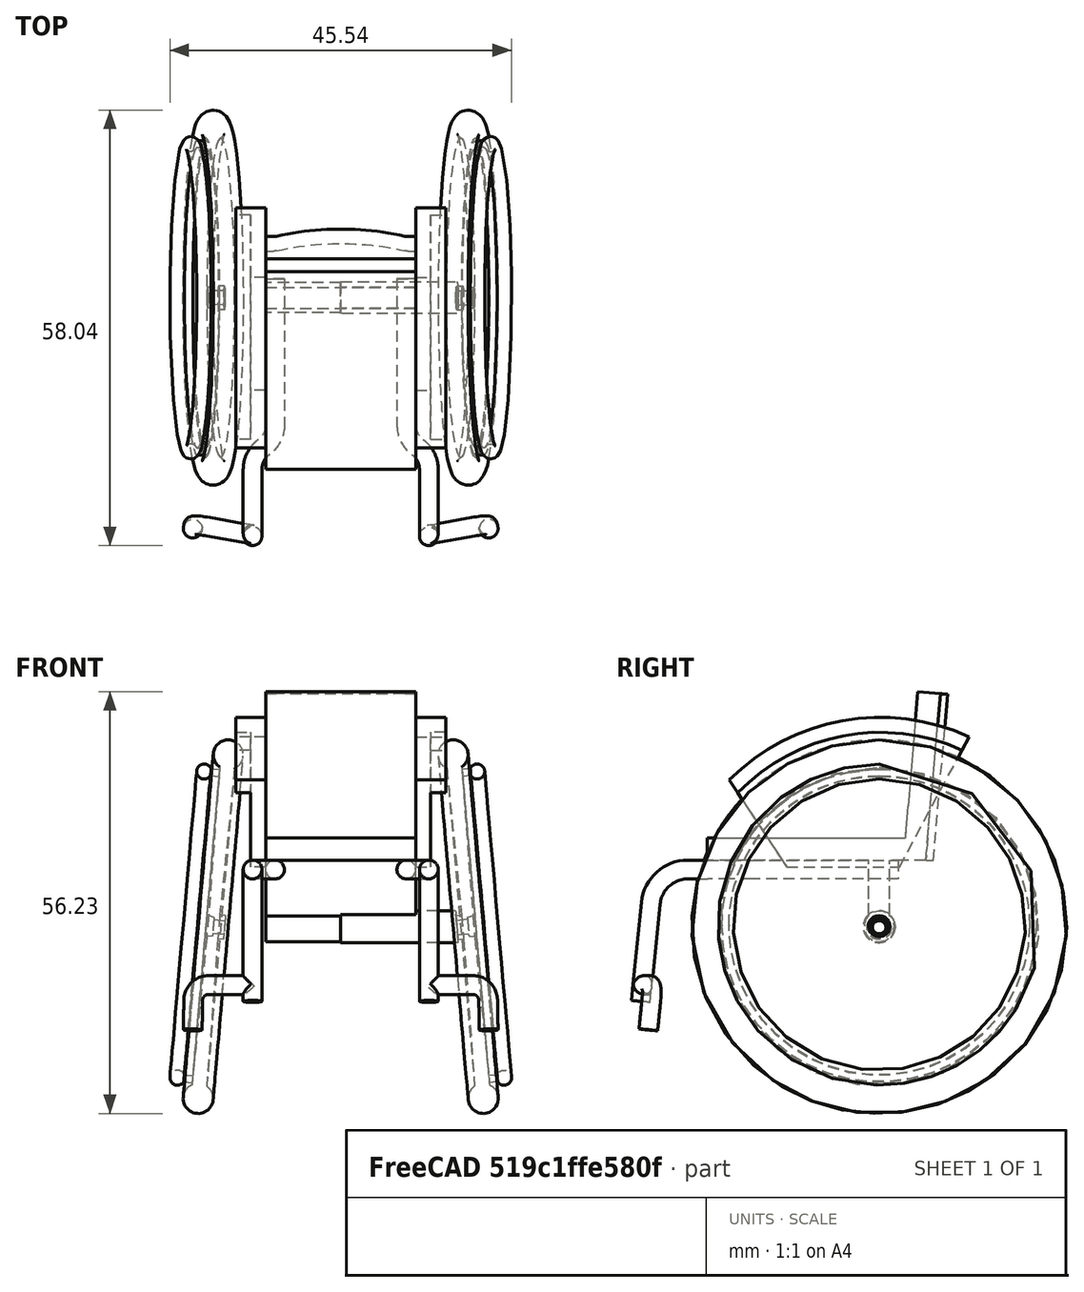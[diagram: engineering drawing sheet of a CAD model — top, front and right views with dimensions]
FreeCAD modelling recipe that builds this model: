
FCSTD DOCUMENT  (FreeCAD 2021.0205R23662 +3201 (Git))
Label: ToyWheelchair_02_mirrored
License: All rights reserved
LicenseURL: http://en.wikipedia.org/wiki/All_rights_reserved
objects: Sketcher::SketchObject×15, PartDesign::Plane×8, PartDesign::Body×5, PartDesign::Pad×5, PartDesign::ShapeBinder×4, PartDesign::AdditivePipe×3, PartDesign::Mirrored×3, PartDesign::Revolution×1, Spreadsheet::Sheet×1, PartDesign::Point×1
note: 66 computed .brp shape members not serialized (recipe doc carries the construction recipe); baked Part::Feature solids carry a one-line shape summary decoded from their .brp

FEATURE [Sketcher::SketchObject] Sketch  label="MASTER.Sketch"
  FullyConstrained = false
  MapMode = 5
  Placement = pos=(0,0,0) rot=(0.57735,0.57735,0.57735;2.0944rad)
  Support = -> [YZ_Plane]
  expr: Constraints[29] = cos(Spreadsheet.WheelAngle) * Spreadsheet.WheelDiameter
  expr: Constraints[36] = Spreadsheet.WheelDiameter
  sketch-geometry (15):
    g0: Circle CenterX=0 CenterY=24.9049 CenterZ=0 NormalX=0 NormalY=0 NormalZ=1 AngleXU=0 Radius=2.63162
    g1: LineSegment StartX=-6.93783 StartY=34.5214 StartZ=0 EndX=28.2394 EndY=34.5214 EndZ=0
    g2: LineSegment StartX=0 StartY=32.5214 StartZ=0 EndX=-25.4861 EndY=32.5214 EndZ=0
    g3: LineSegment StartX=-30.46 StartY=28.031 StartZ=0 EndX=-32 EndY=13 EndZ=0
    g4: LineSegment StartX=-32 StartY=13 StartZ=0 EndX=-29 EndY=5 EndZ=0
    g5: Circle CenterX=-29 CenterY=5 CenterZ=0 NormalX=0 NormalY=0 NormalZ=1 AngleXU=0 Radius=5
    g6: LineSegment [constr] StartX=-29 StartY=5 StartZ=0 EndX=-29 EndY=12.0907 EndZ=0
    g7: ArcOfCircle CenterX=-25.4861 CenterY=27.5214 CenterZ=0 NormalX=0 NormalY=0 NormalZ=1 AngleXU=0 Radius=5 StartAngle=1.5708 EndAngle=3.0395
    g8: LineSegment [constr] StartX=-25.4861 StartY=32.5214 StartZ=0 EndX=-32.1716 EndY=32.5214 EndZ=0
    g9: LineSegment [constr] StartX=-30.46 StartY=28.031 StartZ=0 EndX=-29.1955 EndY=40.3737 EndZ=0
    g10: GeomPoint [constr] X=-30 Y=32.5214 Z=0
    g11: LineSegment StartX=0 StartY=0 StartZ=0 EndX=0 EndY=24.9049 EndZ=0
    g12: LineSegment StartX=0 StartY=24.9049 StartZ=0 EndX=0 EndY=49.8097 EndZ=0
    g13: LineSegment StartX=-25 StartY=24.9049 StartZ=0 EndX=0 EndY=24.9049 EndZ=0
    g14: LineSegment StartX=0 StartY=24.9049 StartZ=0 EndX=25 EndY=24.9049 EndZ=0
  constraints (37):
    c: Horizontal(g1)
    c: DistanceY(g-1,g1) = 34.5214
    c: Horizontal(g2)
    c: Coincident(g4,g3)
    c: Coincident(g5,g4)
    c: Tangent(g5,g-1)
    c: Diameter(g5) = 10
    c: Coincident(g6,g4)
    c: Vertical(g6)
    c: DistanceY(g4,g3) = 8
    c: DistanceX(g3,g4) = 3
    c: Tangent(g2,g7) = -1.5708
    c: Tangent(g3,g7) = -1.5708
    c: Radius(g7) = 5
    c: DistanceY(g2,g1) = 2
    c: PointOnObject(g2,g-2)
    c: Coincident(g8,g2)
    c: Horizontal(g8)
    c: Coincident(g9,g3)
    c: Tangent(g9,g7)
    c: PointOnObject(g10,g8)
    c: PointOnObject(g10,g9)
    c: DistanceX(g10,g-1) = 30
    c: DistanceX(g3,g10) = 2
    c: Coincident(g11,g-1)
    c: Coincident(g11,g0)
    c: Vertical(g11)
    c: Coincident(g12,g0)
    c: PointOnObject(g12,g-2)
    c: Distance(g11,g12) = 49.8097
    c: Coincident(g13,g0)
    c: Horizontal(g13)
    c: Coincident(g14,g0)
    c: Horizontal(g14)
    c: Equal(g12,g11)
    c: Equal(g13,g14)
    c: Distance(g13,g14) = 50
FEATURE [Sketcher::SketchObject] Sketch001  label="Sketch.Wheel.Angle"
  FullyConstrained = true
  MapMode = 5
  Placement = pos=(0,0,0) rot=(1,0,0;1.5708rad)
  Support = -> [XZ_Plane]
  expr: Constraints[4] = Spreadsheet.SeatWidth / 2 + 7
  expr: Constraints[6] = 50mm
  sketch-geometry (3):
    g0: LineSegment StartX=19.1789 StartY=0 StartZ=0 EndX=14.8211 EndY=49.8097 EndZ=0
    g1: Circle [constr] CenterX=17 CenterY=24.9049 CenterZ=0 NormalX=0 NormalY=0 NormalZ=1 AngleXU=0 Radius=25
    g2: GeomPoint [constr] X=14.8211 Y=49.8097 Z=0
  constraints (8):
    c: PointOnObject(g0,g-1)
    c: PointOnObject(g1,g0)
    c: PointOnObject(g0,g1)
    c: PointOnObject(g0,g1)
    c: DistanceX(g-1,g1) = 17
    c: Angle(g-2,g0) = 0.0872665
    c: Distance(g0) = 50
    c: Coincident(g2,g0)
FEATURE [PartDesign::Body] Body  label="MASTER.Body"
  AutoGroupSolids = false
  ExportMode = 0
  Group = -> [Sketch001,Sketch]
  Origin = -> Origin
  _ExportChildren = -> [Sketch001,Sketch]
  _GroupVersion = 1
FEATURE [PartDesign::ShapeBinder] ShapeBinder
  Placement = pos=(0,0,0) rot=(0.57735,0.57735,0.57735;2.0944rad)
  Support = -> [Sketch]
  TraceSupport = false
FEATURE [PartDesign::Plane] DatumPlane
  AttachmentOffset = pos=(0,0,10) rot=(0,0,1;0rad)
  Length = 10
  MapMode = 5
  MinimumLength = 10
  MinimumWidth = 10
  Placement = pos=(10,-2.2e-15,2.2e-15) rot=(0.57735,0.57735,0.57735;2.0944rad)
  ResizeMode = 0
  Support = -> [YZ_Plane001]
  Width = 10
  expr: .AttachmentOffset.Base.z = Spreadsheet.SeatWidth / 2
FEATURE [Sketcher::SketchObject] Sketch002
  ExternalGeometry = -> [ShapeBinder]
  FullyConstrained = false
  MapMode = 5
  Placement = pos=(10,-2.2e-15,2.2e-15) rot=(0.57735,0.57735,0.57735;2.0944rad)
  Support = -> [DatumPlane]
  expr: Constraints[10] = Spreadsheet.WheelDiameter
  sketch-geometry (10):
    g0: LineSegment StartX=-20 StartY=44.4492 StartZ=0 EndX=-12.3537 EndY=32.8577 EndZ=0
    g1: LineSegment StartX=-12.3537 StartY=32.8577 StartZ=0 EndX=2.70695 EndY=32.8577 EndZ=0
    g2: LineSegment StartX=2.70695 StartY=32.8577 StartZ=0 EndX=12 EndY=50.201 EndZ=0
    g3: ArcOfCircle CenterX=0.114642 CenterY=24.4333 CenterZ=0 NormalX=0 NormalY=0 NormalZ=1 AngleXU=0 Radius=28.3767 StartAngle=1.13863 EndAngle=2.35865
    g4: GeomPoint [constr] X=10.3723 Y=47.1634 Z=0
    g5: GeomPoint [constr] X=0 Y=52.8097 Z=0
    g6: Circle [constr] CenterX=1.1e-15 CenterY=24.9049 CenterZ=0 NormalX=0 NormalY=0 NormalZ=1 AngleXU=0 Radius=25
    g7: GeomPoint [constr] X=-18.3252 Y=41.9103 Z=0
    g8: Circle [constr] CenterX=-19.174 CenterY=43.1971 CenterZ=0 NormalX=0 NormalY=0 NormalZ=1 AngleXU=0 Radius=1.5
    g9: Circle [constr] CenterX=11.2916 CenterY=48.8788 CenterZ=0 NormalX=0 NormalY=0 NormalZ=1 AngleXU=0 Radius=1.5
  constraints (23):
    c: Coincident(g0,g1)
    c: Horizontal(g1)
    c: Coincident(g1,g2)
    c: Coincident(g3,g2)
    c: Coincident(g3,g0)
    c: PointOnObject(g4,g2)
    c: PointOnObject(g5,g-2)
    c: PointOnObject(g5,g3)
    c: Distance(g-3,g5) = 3
    c: Coincident(g6,g-3)
    c: Diameter(g6) = 50
    c: PointOnObject(g7,g6)
    c: PointOnObject(g7,g0)
    c: DistanceX(g5,g2) = 12
    c: DistanceX(g0,g5) = 20
    c: PointOnObject(g8,g0)
    c: PointOnObject(g0,g8)
    c: PointOnObject(g9,g2)
    c: PointOnObject(g2,g9)
    c: Tangent(g9,g6)
    c: Tangent(g8,g6)
    c: Equal(g8,g9)
    c: Diameter(g9) = 3
FEATURE [PartDesign::Pad] Pad
  ClaimChildren = false
  Direction = (1,1,1)
  Fit = 0
  FitJoin = 0
  InnerFit = 0
  InnerFitJoin = 0
  InnerTaperAngle = 0
  InnerTaperAngleRev = 0
  Length = 2
  Length2 = 100
  NewSolid = false
  Placement = pos=(10,-2.2e-15,2.2e-15) rot=(0.57735,0.57735,0.57735;2.0944rad)
  Profile = -> Sketch002
  Suppress = false
  Type = 0
FEATURE [PartDesign::ShapeBinder] ShapeBinder001
  Placement = pos=(0,0,0) rot=(1,0,0;1.5708rad)
  Support = -> [Sketch001]
  TraceSupport = false
FEATURE [Sketcher::SketchObject] Sketch003
  ExternalGeometry = -> [ShapeBinder001]
  FullyConstrained = false
  MapMode = 5
  Placement = pos=(0,0,0) rot=(1,0,0;1.5708rad)
  Support = -> [XZ_Plane002]
  sketch-geometry (20):
    g0: Circle [constr] CenterX=17 CenterY=24.9049 CenterZ=0 NormalX=0 NormalY=0 NormalZ=1 AngleXU=0 Radius=25
    g1: ArcOfCircle CenterX=14.9954 CenterY=47.8173 CenterZ=0 NormalX=0 NormalY=0 NormalZ=1 AngleXU=0 Radius=2 StartAngle=5.32325 EndAngle=10.5592
    g2: LineSegment StartX=15.3663 StartY=26.368 StartZ=0 EndX=16.1134 EndY=26.4334 EndZ=0
    g3: LineSegment [constr] StartX=18.3548 StartY=26.6295 StartZ=0 EndX=18.4943 EndY=25.0356 EndZ=0
    g4: LineSegment [constr] StartX=18.4943 StartY=25.0356 StartZ=0 EndX=15.5057 EndY=24.7741 EndZ=0
    g5: LineSegment [constr] StartX=15.5057 StartY=24.7741 StartZ=0 EndX=15.3663 EndY=26.368 EndZ=0
    g6: LineSegment StartX=16.1426 StartY=46.179 StartZ=0 EndX=16.1661 EndY=45.8642 EndZ=0
    g7: LineSegment StartX=14.1502 StartY=46.0047 StartZ=0 EndX=16.1134 EndY=26.4334 EndZ=0
    g8: ArcOfCircle CenterX=18.2028 CenterY=45.5778 CenterZ=0 NormalX=0 NormalY=0 NormalZ=1 AngleXU=0 Radius=1 StartAngle=3.71006 EndAngle=9.03084
    g9: LineSegment [constr] StartX=18.2028 StartY=45.5778 StartZ=0 EndX=15.2142 EndY=45.3163 EndZ=0
    g10: LineSegment StartX=17.2794 StartY=45.9616 StartZ=0 EndX=16.1661 EndY=45.8642 EndZ=0
    g11: LineSegment StartX=17.3601 StartY=45.0395 StartZ=0 EndX=16.235 EndY=44.941 EndZ=0
    g12: LineSegment StartX=16.235 StartY=44.941 StartZ=0 EndX=17.6077 EndY=26.5641 EndZ=0
    g13: LineSegment [constr] StartX=16.1661 StartY=45.8642 StartZ=0 EndX=16.235 EndY=44.941 EndZ=0
    g14: LineSegment StartX=16.8909 StartY=26.1514 StartZ=0 EndX=16.916 EndY=25.8649 EndZ=0
    g15: LineSegment StartX=16.916 StartY=25.8649 StartZ=0 EndX=15.4261 EndY=25.6845 EndZ=0
    g16: LineSegment StartX=15.4261 StartY=25.6845 StartZ=0 EndX=15.3663 EndY=26.368 EndZ=0
    g17: LineSegment StartX=16.8909 StartY=26.1514 StartZ=0 EndX=17.6214 EndY=26.3806 EndZ=0
    g18: LineSegment StartX=17.6077 StartY=26.5641 StartZ=0 EndX=17.6214 EndY=26.3806 EndZ=0
    g19: LineSegment [constr] StartX=15.3663 StartY=26.368 StartZ=0 EndX=18.3548 EndY=26.6295 EndZ=0
  constraints (54):
    c: PointOnObject(g0,g-3)
    c: PointOnObject(g-3,g0)
    c: PointOnObject(g-3,g0)
    c: PointOnObject(g-3,g1)
    c: Coincident(g3,g4)
    c: Coincident(g4,g5)
    c: Coincident(g5,g2)
    c: PointOnObject(g0,g4)
    c: Perpendicular(g5,g4)
    c: Perpendicular(g-3,g4)
    c: Perpendicular(g3,g4)
    c: Symmetric(g2,g3,g-3)
    c: Symmetric(g7,g12,g-3)
    c: Symmetric(g6,g7,g-3)
    c: Coincident(g1,g6)
    c: Coincident(g1,g7)
    c: PointOnObject(g2,g7)
    c: Diameter(g1) = 4
    c: Distance(g1,g1) = 2
    c: Distance(g2,g12) = 1.5
    c: Distance(g2,g3) = 3
    c: Distance(g3) = 1.6
    c: Diameter(g8) = 2
    c: Coincident(g9,g8)
    c: PointOnObject(g9,g-3)
    c: Perpendicular(g-3,g9)
    c: Distance(g9) = 3
    c: Parallel(g9,g10)
    c: Parallel(g9,g11)
    c: Symmetric(g11,g10,g9)
    c: Coincident(g8,g10)
    c: PointOnObject(g8,g11)
    c: Coincident(g12,g11)
    c: Tangent(g6,g12)
    c: Coincident(g6,g10)
    c: Coincident(g13,g6)
    c: Coincident(g13,g11)
    c: PointOnObject(g14,g-3)
    c: PointOnObject(g14,g-3)
    c: Coincident(g14,g15)
    c: PointOnObject(g15,g5)
    c: Coincident(g15,g16)
    c: Coincident(g16,g2)
    c: Distance(g4,g15) = 0.913816
    c: Distance(g14,g0) = 0.963725
    c: Distance(g0,g14) = 1.25134
    c: Coincident(g17,g14)
    c: Coincident(g18,g12)
    c: Coincident(g18,g17)
    c: Parallel(g12,g18)
    c: Coincident(g19,g2)
    c: Coincident(g19,g3)
    c: PointOnObject(g12,g19)
    c: PointOnObject(g2,g19)
FEATURE [Sketcher::SketchObject] Sketch004
  ExternalGeometry = -> [ShapeBinder001]
  FullyConstrained = true
  MapMode = 5
  Placement = pos=(0,0,0) rot=(1,0,0;1.5708rad)
  Support = -> [XZ_Plane002]
  sketch-geometry (3):
    g0: Circle [constr] CenterX=17 CenterY=24.9049 CenterZ=0 NormalX=0 NormalY=0 NormalZ=1 AngleXU=0 Radius=25
    g1: LineSegment StartX=17 StartY=24.9049 StartZ=0 EndX=41.9049 EndY=27.0838 EndZ=0
    g2: LineSegment StartX=17 StartY=24.9049 StartZ=0 EndX=-7.90487 EndY=22.726 EndZ=0
  constraints (9):
    c: PointOnObject(g0,g-3)
    c: PointOnObject(g-3,g0)
    c: PointOnObject(g-3,g0)
    c: Coincident(g1,g0)
    c: PointOnObject(g1,g0)
    c: Perpendicular(g-3,g1)
    c: Coincident(g2,g1)
    c: PointOnObject(g2,g0)
    c: Parallel(g1,g2)
FEATURE [PartDesign::Revolution] Revolution
  Angle = 360
  Axis = (0.996195,0,0.0871557)
  Base = (17,-5.5e-15,24.9049)
  ClaimChildren = false
  Fit = 0
  FitJoin = 0
  InnerFit = 0
  InnerFitJoin = 0
  NewSolid = false
  Placement = pos=(0,0,0) rot=(1,0,0;1.5708rad)
  Profile = -> Sketch003
  ReferenceAxis = -> Sketch004 [Edge2]
  Reversed = true
  Suppress = false
FEATURE [Spreadsheet::Sheet] Spreadsheet
  PythonMode = false
  cells = A1=SeatWidth; B1(SeatWidth)==20mm; A2=WheelDiameter; B2(WheelDiameter)==50mm; A3=TireDiameter; B3(TireDiameter)==2mm; A4=SeatHeight; B4(SeatHeight)==40mm; A5=WheelAngle; B5(WheelAngle)==5deg; A6=SeatAngle; B6(SeatAngle)==5deg; A7=TubeDiameter; B7(TubeDiameter)==2.5mm; A8=TubeCurveOffset; B8(TubeCurveOffset)==3mm; A9=AxleDiameter; B9(AxleDiameter)==4mm
FEATURE [PartDesign::ShapeBinder] ShapeBinder002
  Placement = pos=(0,0,0) rot=(0.57735,0.57735,0.57735;2.0944rad)
  Support = -> [Sketch]
  TraceSupport = false
FEATURE [Sketcher::SketchObject] Sketch005
  ExternalGeometry = -> [ShapeBinder002]
  FullyConstrained = false
  MapMode = 5
  Placement = pos=(0,0,0) rot=(0.57735,0.57735,0.57735;2.0944rad)
  Support = -> [YZ_Plane003]
  sketch-geometry (11):
    g0: ArcOfCircle CenterX=-5.5e-15 CenterY=24.9049 CenterZ=0 NormalX=0 NormalY=0 NormalZ=1 AngleXU=0 Radius=2 StartAngle=2.34619 EndAngle=7.07858
    g1: LineSegment StartX=6.47551 StartY=36.7159 StartZ=0 EndX=6.2142 EndY=33.7159 EndZ=0
    g2: LineSegment StartX=6.2142 StartY=33.7159 StartZ=0 EndX=1.4 EndY=33.7159 EndZ=0
    g3: LineSegment StartX=-22.9045 StartY=33.7159 StartZ=0 EndX=-22.9045 EndY=36.7159 EndZ=0
    g4: LineSegment StartX=1.4 StartY=26.3332 StartZ=0 EndX=1.4 EndY=33.7159 EndZ=0
    g5: LineSegment StartX=-1.4 StartY=26.3332 StartZ=0 EndX=-1.4 EndY=33.7159 EndZ=0
    g6: LineSegment StartX=-1.4 StartY=33.7159 StartZ=0 EndX=-22.9045 EndY=33.7159 EndZ=0
    g7: LineSegment StartX=-22.9045 StartY=36.7159 StartZ=0 EndX=3.46416 EndY=36.7159 EndZ=0
    g8: LineSegment StartX=6.47551 StartY=36.7159 StartZ=0 EndX=8.15211 EndY=55.9642 EndZ=0
    g9: LineSegment StartX=8.15211 StartY=55.9642 StartZ=0 EndX=5.16342 EndY=56.2245 EndZ=0
    g10: LineSegment StartX=5.16342 StartY=56.2245 StartZ=0 EndX=3.46416 EndY=36.7159 EndZ=0
  constraints (27):
    c: Coincident(g0,g-3)
    c: Symmetric(g0,g0,g-2)
    c: Diameter(g0) = 4
    c: DistanceX(g0,g0) = 2.8
    c: Coincident(g1,g2)
    c: Horizontal(g2)
    c: Coincident(g6,g3)
    c: Vertical(g3)
    c: Coincident(g4,g0)
    c: Vertical(g4)
    c: Coincident(g5,g0)
    c: Vertical(g5)
    c: Coincident(g2,g4)
    c: Coincident(g6,g5)
    c: Tangent(g2,g6)
    c: DistanceY(g1,g1) = 3
    c: Coincident(g7,g3)
    c: Horizontal(g7)
    c: Coincident(g8,g1)
    c: Coincident(g9,g8)
    c: Coincident(g10,g9)
    c: Coincident(g7,g10)
    c: DistanceY(g3,g3) = 3
    c: Equal(g3,g9)
    c: Perpendicular(g10,g9)
    c: Perpendicular(g8,g9)
    c: Parallel(g8,g1)
FEATURE [PartDesign::Pad] Pad001
  ClaimChildren = false
  Direction = (1,1,1)
  Fit = 0
  FitJoin = 0
  InnerFit = 0
  InnerFitJoin = 0
  InnerTaperAngle = 0
  InnerTaperAngleRev = 0
  Length = 20
  Length2 = 100
  Midplane = true
  NewSolid = false
  Placement = pos=(0,0,0) rot=(0.57735,0.57735,0.57735;2.0944rad)
  Profile = -> Sketch005
  Suppress = false
  Type = 0
  expr: Length = Spreadsheet.SeatWidth
FEATURE [PartDesign::Plane] DatumPlane001
  AttachmentOffset = pos=(0,0,11.75) rot=(0,0,1;0rad)
  Length = 10
  MapMode = 5
  MinimumLength = 10
  MinimumWidth = 10
  Placement = pos=(11.75,-2.6e-15,2.6e-15) rot=(0.57735,0.57735,0.57735;2.0944rad)
  ResizeMode = 0
  Support = -> [YZ_Plane004]
  Width = 10
  expr: .AttachmentOffset.Base.z = Spreadsheet.SeatWidth / 2 + Spreadsheet.TubeCurveOffset - Spreadsheet.TubeDiameter / 2
FEATURE [PartDesign::ShapeBinder] ShapeBinder003
  Placement = pos=(0,0,0) rot=(0.57735,0.57735,0.57735;2.0944rad)
  Support = -> [Sketch]
  TraceSupport = false
FEATURE [Sketcher::SketchObject] Sketch006  label="Sketch.TubeBottom"
  ExternalGeometry = -> [ShapeBinder003]
  FullyConstrained = false
  MapMode = 5
  Placement = pos=(11.75,-2.6e-15,2.6e-15) rot=(0.57735,0.57735,0.57735;2.0944rad)
  Support = -> [DatumPlane001]
  sketch-geometry (3):
    g0: LineSegment StartX=-25.4861 StartY=32.5214 StartZ=0 EndX=-23.8778 EndY=32.5214 EndZ=0
    g1: LineSegment StartX=-30.46 StartY=28.031 StartZ=0 EndX=-31.5781 EndY=17.1179 EndZ=0
    g2: LineSegment StartX=-31.5781 StartY=17.1179 StartZ=0 EndX=-31.8014 EndY=14.9385 EndZ=0
  constraints (6):
    c: Coincident(g0,g-3)
    c: Horizontal(g0)
    c: Coincident(g1,g-4)
    c: PointOnObject(g1,g-4)
    c: Coincident(g2,g1)
    c: PointOnObject(g2,g-4)
FEATURE [PartDesign::Plane] DatumPlane002
  Length = 11.75
  MapMode = 6
  MinimumLength = 10
  MinimumWidth = 10
  Placement = pos=(11.75,-23.8778,32.5214) rot=(0,0,1;3.14159rad)
  ResizeMode = 0
  Support = -> [Sketch006,XY_Plane004]
  Width = 23.8778
FEATURE [PartDesign::Plane] DatumPlane003
  Length = 32.5214
  MapMode = 6
  MinimumLength = 10
  MinimumWidth = 10
  Placement = pos=(11.75,-23.8778,32.5214) rot=(0.57735,-0.57735,0.57735;2.0944rad)
  ResizeMode = 0
  Support = -> [Sketch006,XZ_Plane004]
  Width = 11.75
FEATURE [Sketcher::SketchObject] Sketch007  label="Sketch.TubeProfile"
  FullyConstrained = true
  MapMode = 5
  Placement = pos=(11.75,-23.8778,32.5214) rot=(-0.57735,0.57735,-0.57735;4.18879rad)
  Support = -> [DatumPlane003]
  sketch-geometry (1):
    g0: Circle CenterX=0 CenterY=0 CenterZ=0 NormalX=0 NormalY=0 NormalZ=1 AngleXU=0 Radius=1.25
  constraints (2):
    c: Coincident(g0,g-1)
    c: Diameter(g0) = 2.5
FEATURE [Sketcher::SketchObject] Sketch008  label="Sketch.TubeTop"
  FullyConstrained = false
  MapMode = 5
  Placement = pos=(11.75,-23.8778,32.5214) rot=(0,0,1;3.14159rad)
  Support = -> [DatumPlane002]
  expr: Constraints[11] = Spreadsheet.TubeCurveOffset
  expr: Constraints[8] = Spreadsheet.TubeDiameter
  sketch-geometry (5):
    g0: LineSegment StartX=0 StartY=0 StartZ=0 EndX=0 EndY=-1 EndZ=0
    g1: ArcOfCircle CenterX=3.6638 CenterY=-1 CenterZ=0 NormalX=0 NormalY=0 NormalZ=1 AngleXU=0 Radius=3.6638 StartAngle=3.14159 EndAngle=4.0806
    g2: ArcOfCircle CenterX=-0.663796 CenterY=-6.91317 CenterZ=0 NormalX=0 NormalY=0 NormalZ=1 AngleXU=0 Radius=3.6638 StartAngle=6.28319 EndAngle=7.2222
    g3: LineSegment StartX=3 StartY=-6.91317 StartZ=0 EndX=3 EndY=-26.4 EndZ=0
    g4: Circle [constr] CenterX=0 CenterY=0 CenterZ=0 NormalX=0 NormalY=0 NormalZ=1 AngleXU=0 Radius=1.25
  constraints (15):
    c: Coincident(g0,g-1)
    c: Vertical(g0)
    c: Coincident(g1,g0)
    c: Tangent(g1,g-2)
    c: Coincident(g2,g1)
    c: Coincident(g3,g2)
    c: Vertical(g3)
    c: Coincident(g4,g0)
    c: Diameter(g4) = 2.5
    c: Tangent(g2,g3)
    c: DistanceY(g3,g0) = 26.4
    c: DistanceX(g0,g3) = 3
    c: Tangent(g1,g2)
    c: Equal(g1,g2)
    c: DistanceY(g0,g0) = 1
FEATURE [Sketcher::SketchObject] Sketch009
  ExternalGeometry = -> [Pad]
  FullyConstrained = true
  MapMode = 5
  Placement = pos=(12,-2.2e-15,2.4e-15) rot=(0.57735,0.57735,0.57735;2.0944rad)
  Support = -> [Pad]
  sketch-geometry (3):
    g0: LineSegment StartX=-20 StartY=44.4492 StartZ=0 EndX=-18.8756 EndY=42.7446 EndZ=0
    g1: LineSegment StartX=12 StartY=50.201 StartZ=0 EndX=11.0554 EndY=48.4381 EndZ=0
    g2: ArcOfCircle CenterX=0.114642 CenterY=24.4333 CenterZ=0 NormalX=0 NormalY=0 NormalZ=1 AngleXU=0 Radius=26.3805 StartAngle=1.14315 EndAngle=2.37439
  constraints (8):
    c: Coincident(g0,g-4)
    c: PointOnObject(g0,g-4)
    c: Coincident(g1,g-5)
    c: PointOnObject(g1,g-5)
    c: Coincident(g2,g-3)
    c: Coincident(g2,g1)
    c: Coincident(g2,g0)
    c: Distance(g1) = 2
FEATURE [PartDesign::Pad] Pad002
  BaseFeature = -> Pad
  ClaimChildren = false
  Direction = (1,1,1)
  Fit = 0
  FitJoin = 0
  InnerFit = 0
  InnerFitJoin = 0
  InnerTaperAngle = 0
  InnerTaperAngleRev = 0
  Length = 2
  Length2 = 100
  NewSolid = false
  Placement = pos=(10,-2.2e-15,2.2e-15) rot=(0.57735,0.57735,0.57735;2.0944rad)
  Profile = -> Sketch009
  Suppress = false
  Type = 0
FEATURE [PartDesign::Plane] DatumPlane004
  Length = 11.75
  MapMode = 1
  MinimumLength = 10
  MinimumWidth = 10
  Placement = pos=(11.75,-31.5781,17.1179) rot=(0,0,1;0rad)
  ResizeMode = 0
  Support = -> [Sketch006]
  Width = 31.5781
FEATURE [Sketcher::SketchObject] Sketch010
  FullyConstrained = true
  MapMode = 5
  Placement = pos=(11.75,-31.5781,17.1179) rot=(0,0,1;0rad)
  Support = -> [DatumPlane004]
  sketch-geometry (1):
    g0: LineSegment StartX=0 StartY=0 StartZ=0 EndX=4.92404 EndY=0.868241 EndZ=0
  constraints (3):
    c: Coincident(g0,g-1)
    c: Angle(g-1,g0) = 0.174533
    c: Distance(g0) = 5
FEATURE [PartDesign::Point] DatumPoint
  AttacherType = Attacher::AttachEnginePoint
  MapMode = 37
  Placement = pos=(11.75,-31.5781,17.1179) rot=(0,0,1;0rad)
  Support = -> [Sketch006]
FEATURE [PartDesign::Plane] DatumPlane005
  Length = 17.055
  MapMode = 13
  MinimumLength = 10
  MinimumWidth = 10
  Placement = pos=(13.3913,-30.916,20.7556) rot=(0.991599,0.086754,0.095947;1.47864rad)
  ResizeMode = 0
  Support = -> [Sketch010,Sketch006]
  Width = 20.6876
FEATURE [Sketcher::SketchObject] Sketch011
  ExternalGeometry = -> [Sketch010]
  FullyConstrained = true
  MapMode = 5
  Placement = pos=(13.3913,-30.916,20.7556) rot=(0.991599,0.086754,0.095947;1.47864rad)
  Support = -> [DatumPlane005]
  sketch-geometry (3):
    g0: LineSegment StartX=-1.73138 StartY=-3.65616 StartZ=0 EndX=4.26863 EndY=-3.65616 EndZ=0
    g1: LineSegment StartX=6.26862 StartY=-5.65616 StartZ=0 EndX=6.26862 EndY=-9.65616 EndZ=0
    g2: ArcOfCircle CenterX=4.26862 CenterY=-5.65616 CenterZ=0 NormalX=0 NormalY=0 NormalZ=1 AngleXU=0 Radius=2 StartAngle=4.27302e-08 EndAngle=1.57079
  constraints (10):
    c: Coincident(g0,g-3)
    c: PointOnObject(g0,g-3)
    c: Vertical(g1)
    c: Coincident(g2,g0)
    c: Coincident(g2,g1)
    c: Tangent(g2,g1)
    c: Radius(g2) = 2
    c: DistanceY(g1,g0) = 6
    c: DistanceX(g0,g1) = 8
    c: Tangent(g2,g0)
FEATURE [PartDesign::Plane] DatumPlane006
  Length = 10
  MapMode = 7
  MinimumLength = 10
  MinimumWidth = 10
  Placement = pos=(11.75,-31.5781,17.1179) rot=(0.6444,-0.540716,-0.540716;1.99673rad)
  ResizeMode = 0
  Support = -> [Sketch010]
  Width = 10
FEATURE [Sketcher::SketchObject] Sketch012
  FullyConstrained = true
  MapMode = 5
  Placement = pos=(11.75,-31.5781,17.1179) rot=(0.6444,-0.540716,-0.540716;1.99673rad)
  Support = -> [DatumPlane006]
  expr: Constraints[1] = Spreadsheet.TubeDiameter
  sketch-geometry (1):
    g0: Circle CenterX=0 CenterY=0 CenterZ=0 NormalX=0 NormalY=0 NormalZ=1 AngleXU=0 Radius=1.25
  constraints (2):
    c: Coincident(g0,g-1)
    c: Diameter(g0) = 2.5
FEATURE [PartDesign::AdditivePipe] AdditivePipe
  AuxilleryCurvelinear = true
  AuxillerySpineTangent = false
  Binormal = (0,0,0)
  ClaimChildren = false
  Fit = 0
  FitJoin = 0
  InnerFit = 0
  InnerFitJoin = 0
  Mode = 0
  NewSolid = false
  Placement = pos=(11.75,-23.8778,32.5214) rot=(0.57735,-0.57735,0.57735;2.0944rad)
  Profile = -> Sketch007
  Spine = -> Sketch008 [Edge1,Edge2,Edge3,Edge4]
  SpineTangent = false
  Suppress = false
  Transformation = 0
  Transition = 0
FEATURE [PartDesign::AdditivePipe] AdditivePipe001
  AuxilleryCurvelinear = true
  AuxillerySpineTangent = false
  BaseFeature = -> AdditivePipe
  Binormal = (0,0,0)
  ClaimChildren = false
  Fit = 0
  FitJoin = 0
  InnerFit = 0
  InnerFitJoin = 0
  Mode = 0
  NewSolid = false
  Placement = pos=(11.75,-23.8778,32.5214) rot=(0.57735,-0.57735,0.57735;2.0944rad)
  Profile = -> Sketch007
  Spine = -> Sketch006 [Edge4,Edge3,Edge2,Edge1]
  SpineTangent = false
  Suppress = false
  Transformation = 0
  Transition = 0
FEATURE [PartDesign::AdditivePipe] AdditivePipe002
  AuxilleryCurvelinear = true
  AuxillerySpineTangent = false
  BaseFeature = -> AdditivePipe001
  Binormal = (0,0,0)
  ClaimChildren = false
  Fit = 0
  FitJoin = 0
  InnerFit = 0
  InnerFitJoin = 0
  Mode = 0
  NewSolid = false
  Placement = pos=(11.75,-23.8778,32.5214) rot=(0.57735,-0.57735,0.57735;2.0944rad)
  Profile = -> Sketch012
  Spine = -> Sketch011 [Edge1,Edge2,Edge3]
  SpineTangent = false
  Suppress = false
  Transformation = 0
  Transition = 0
FEATURE [Sketcher::SketchObject] Sketch013
  ExternalGeometry = -> [Pad001]
  FullyConstrained = true
  MapMode = 5
  Placement = pos=(-1.36e-14,4.89935,56.2475) rot=(-0.043388,-0.043388,-0.998116;1.57268rad)
  Support = -> [Pad001]
  sketch-geometry (13):
    g0: LineSegment StartX=-3.26507 StartY=10 StartZ=0 EndX=-3.26507 EndY=9 EndZ=0
    g1: ArcOfCircle CenterX=-5.26507 CenterY=8.99998 CenterZ=0 NormalX=0 NormalY=0 NormalZ=1 AngleXU=0 Radius=2 StartAngle=6.06187 EndAngle=6.28319
    g2: LineSegment StartX=-3.26507 StartY=-10 StartZ=0 EndX=-3.26507 EndY=-9 EndZ=0
    g3: ArcOfCircle CenterX=-5.26507 CenterY=-9 CenterZ=0 NormalX=0 NormalY=0 NormalZ=1 AngleXU=0 Radius=2 StartAngle=2.00064e-08 EndAngle=0.221313
    g4: ArcOfCircle CenterX=34.7348 CenterY=-9.2494e-06 CenterZ=0 NormalX=0 NormalY=0 NormalZ=1 AngleXU=0 Radius=38.9999 StartAngle=2.92028 EndAngle=3.36291
    g5: GeomPoint [constr] X=-4.26507 Y=0 Z=0
    g6: GeomPoint [constr] X=-3.26507 Y=0 Z=0
    g7: Circle [constr] CenterX=-3.26507 CenterY=-10 CenterZ=0 NormalX=0 NormalY=0 NormalZ=1 AngleXU=0 Radius=1
    g8: Circle [constr] CenterX=-0.265068 CenterY=-10 CenterZ=0 NormalX=0 NormalY=0 NormalZ=1 AngleXU=0 Radius=1
    g9: BSplineCurve PolesCount=2 KnotsCount=2 Degree=1 IsPeriodic=0
    g10: GeomPoint [constr] X=-3.26507 Y=-10 Z=0
    g11: GeomPoint [constr] X=-0.265068 Y=-10 Z=0
    g12: LineSegment StartX=-3.26507 StartY=10 StartZ=0 EndX=-0.265068 EndY=10 EndZ=0
  constraints (31):
    c: Coincident(g0,g-4)
    c: PointOnObject(g0,g-4)
    c: Coincident(g1,g0)
    c: Tangent(g0,g1)
    c: Coincident(g2,g-4)
    c: PointOnObject(g2,g-4)
    c: Coincident(g3,g2)
    c: Tangent(g3,g-4)
    c: Coincident(g4,g3)
    c: Coincident(g4,g1)
    c: Distance(g0,g0) = 1
    c: Equal(g2,g0)
    c: Equal(g1,g3)
    c: Tangent(g4,g1)
    c: Tangent(g3,g4)
    c: Radius(g3) = 2
    c: PointOnObject(g5,g-1)
    c: PointOnObject(g5,g4)
    c: PointOnObject(g6,g-1)
    c: PointOnObject(g6,g-4)
    c: Distance(g6,g5) = 1
    c: Coincident(g9,g2)
    c: Weight(g7) = 1
    c: Equal(g7,g8)
    c: InternalAlignment(g7,g9)
    c: InternalAlignment(g8,g9)
    c: InternalAlignment(g10,g9)
    c: InternalAlignment(g11,g9)
    c: Coincident(g12,g0)
    c: Coincident(g12,g-3)
    c: Coincident(g9,g-3)
FEATURE [PartDesign::Pad] Pad003
  BaseFeature = -> Pad001
  ClaimChildren = false
  Direction = (1,1,1)
  Fit = 0
  FitJoin = 0
  InnerFit = 0
  InnerFitJoin = 0
  InnerTaperAngle = 0
  InnerTaperAngleRev = 0
  Length = 10
  Length2 = 100
  NewSolid = false
  Placement = pos=(0,0,0) rot=(0.57735,0.57735,0.57735;2.0944rad)
  Profile = -> Sketch013
  Suppress = false
  Type = 3
  UpToFace = -> Pad001 [Face3]
FEATURE [PartDesign::Plane] DatumPlane007
  Length = 53.6016
  MapMode = 5
  MinimumLength = 10
  MinimumWidth = 10
  Placement = pos=(17.5389,0,1.53446) rot=(0.737277,0,-0.67559;3.14159rad)
  ResizeMode = 0
  Support = -> [Revolution]
  Width = 49.9903
FEATURE [Sketcher::SketchObject] Sketch014
  ExternalGeometry = -> [ShapeBinder002]
  FullyConstrained = true
  MapMode = 5
  Placement = pos=(0,0,0) rot=(0.57735,0.57735,0.57735;2.0944rad)
  Support = -> [YZ_Plane003]
  expr: Constraints[1] = Spreadsheet.AxleDiameter
  sketch-geometry (1):
    g0: Circle CenterX=0 CenterY=24.9049 CenterZ=0 NormalX=0 NormalY=0 NormalZ=1 AngleXU=0 Radius=2
  constraints (2):
    c: Coincident(g0,g-3)
    c: Diameter(g0) = 4
FEATURE [PartDesign::Pad] Pad004
  BaseFeature = -> Pad003
  ClaimChildren = false
  Direction = (1,1,1)
  Fit = 0
  FitJoin = 0
  InnerFit = 0
  InnerFitJoin = 0
  InnerTaperAngle = 0
  InnerTaperAngleRev = 0
  Length = 10
  Length2 = 100
  NewSolid = false
  Placement = pos=(0,0,0) rot=(0.57735,0.57735,0.57735;2.0944rad)
  Profile = -> Sketch014
  Suppress = false
  Type = 3
  UpToFace = -> Sketch014
FEATURE [PartDesign::Body] Body003  label="Body.AxleSeat"
  AutoGroupSolids = false
  ExportMode = 0
  Group = -> [ShapeBinder002,Sketch005,Pad001,Sketch013,Pad003,Sketch014,Pad004]
  Origin = -> Origin003
  Tip = -> Pad004
  _ExportChildren = -> [ShapeBinder002,Pad001,Pad003,Pad004]
  _GroupVersion = 1
FEATURE [PartDesign::Mirrored] Mirrored
  BaseFeature = -> Revolution
  CopyShape = false
  MirrorPlane = -> Sketch003 [V_Axis]
  NewSolid = false
  OriginalSubs = -> [Revolution]
  Originals = -> [Revolution]
  Placement = pos=(0,0,0) rot=(1,0,0;1.5708rad)
  SubTransform = true
  Suppress = false
FEATURE [PartDesign::Body] Body002  label="Body.Wheel"
  AutoGroupSolids = false
  ExportMode = 0
  Group = -> [ShapeBinder001,Sketch003,Sketch004,Revolution,DatumPlane007,Mirrored]
  Origin = -> Origin002
  Tip = -> Mirrored
  _ExportChildren = -> [ShapeBinder001,Sketch004,Revolution,DatumPlane007,Mirrored]
  _GroupVersion = 1
FEATURE [PartDesign::Mirrored] Mirrored001
  BaseFeature = -> Pad002
  CopyShape = false
  MirrorPlane = -> YZ_Plane001
  NewSolid = false
  OriginalSubs = -> [Pad,Pad002]
  Originals = -> [Pad,Pad002]
  Placement = pos=(10,-2.2e-15,2.2e-15) rot=(0.57735,0.57735,0.57735;2.0944rad)
  SubTransform = true
  Suppress = false
FEATURE [PartDesign::Body] Body001  label="Body.SidePanel"
  AutoGroupSolids = false
  ExportMode = 0
  Group = -> [ShapeBinder,DatumPlane,Sketch002,Pad,Sketch009,Pad002,Mirrored001]
  Origin = -> Origin001
  Tip = -> Mirrored001
  _ExportChildren = -> [ShapeBinder,DatumPlane,Pad,Pad002,Mirrored001]
  _GroupVersion = 1
FEATURE [PartDesign::Mirrored] Mirrored002
  BaseFeature = -> AdditivePipe002
  CopyShape = false
  MirrorPlane = -> YZ_Plane004
  NewSolid = false
  OriginalSubs = -> [AdditivePipe001,AdditivePipe002,AdditivePipe]
  Originals = -> [AdditivePipe001,AdditivePipe002,AdditivePipe]
  Placement = pos=(11.75,-23.8778,32.5214) rot=(0.57735,-0.57735,0.57735;2.0944rad)
  SubTransform = true
  Suppress = false
FEATURE [PartDesign::Body] Body004  label="Body.Tube"
  AutoGroupSolids = false
  ExportMode = 0
  Group = -> [DatumPlane001,ShapeBinder003,Sketch006,DatumPlane002,DatumPlane003,Sketch007,Sketch008,AdditivePipe,DatumPlane004,Sketch010,DatumPoint,DatumPlane005,Sketch011,DatumPlane006,Sketch012,AdditivePipe001,AdditivePipe002,Mirrored002]
  Origin = -> Origin004
  Tip = -> Mirrored002
  _ExportChildren = -> [DatumPlane001,ShapeBinder003,DatumPlane002,DatumPlane003,AdditivePipe,DatumPlane004,Sketch010,DatumPoint,DatumPlane005,DatumPlane006,AdditivePipe001,AdditivePipe002,Mirrored002]
  _GroupVersion = 1
